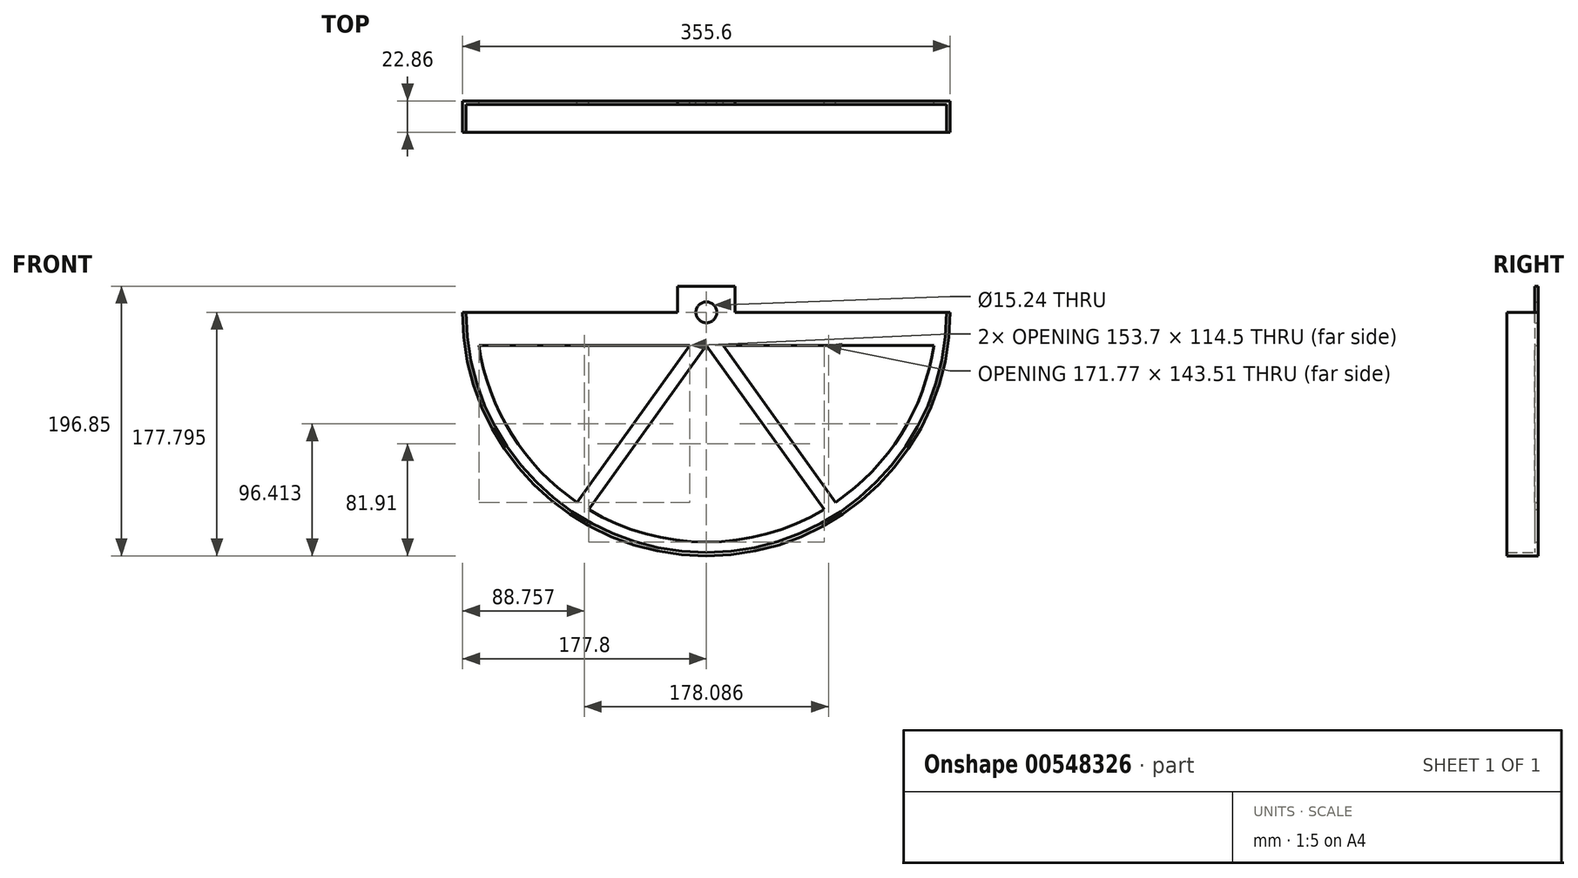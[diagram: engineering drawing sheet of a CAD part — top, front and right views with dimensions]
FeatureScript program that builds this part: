
annotation { "Feature Type Name" : "Feature", "Feature Type Description" : "" }
export const myFeature = defineFeature(function(context is Context, id is Id, definition is map)
    precondition{}
    {
        {
            var Q0;
            Q0=qCreatedBy(makeId("Front.planeOp"),FACE);
            var sketch = newSketch(context, id + "F0", { "sketchPlane" : qUnion([Q0])});
            skArc(sketch, "E0", {"start": v(-177.8, 177.3) * mm, "mid": v(0, -0.5) * mm, "end": v(177.8, 177.3) * mm});
            skLineSegment(sketch, "E1", {"start": v(0, 177.3) * mm, "end": v(177.8, 177.3) * mm});
            skLineSegment(sketch, "E2", {"start": v(0, 177.3) * mm, "end": v(-177.8, 177.3) * mm});
            skLineSegment(sketch, "E3.MirrorCS", {"start": v(-142.3, 159.18) * mm, "end": v(-142.3, 161.09) * mm});
            skLineSegment(sketch, "E4.MirrorCS", {"start": v(-166, 159.36) * mm, "end": v(-166.07, 161.26) * mm});
            skArc(sketch, "E5.MirrorCS", {"start": v(-169.1, 155.45) * mm, "mid": v(-160.47, 148.66) * mm, "end": v(-157.47, 159.21) * mm});
            skLineSegment(sketch, "E6.MirrorCS", {"start": v(-170.16, 157.27) * mm, "end": v(-168.5, 159.37) * mm});
            skLineSegment(sketch, "E7.MirrorCS", {"start": v(-174.1, 159.4) * mm, "end": v(-168.5, 159.37) * mm});
            skLineSegment(sketch, "E8.MirrorCS", {"start": v(-155.76, 159.25) * mm, "end": v(-142.3, 159.18) * mm});
            skLineSegment(sketch, "E9.MirrorCS", {"start": v(-142.3, 161.09) * mm, "end": v(-157.54, 161.16) * mm});
            skArc(sketch, "E10.MirrorCS", {"start": v(-170.16, 157.27) * mm, "mid": v(-161.42, 147.02) * mm, "end": v(-155.76, 159.25) * mm});
            skLineSegment(sketch, "E11.MirrorCS", {"start": v(-166.07, 161.26) * mm, "end": v(-174.53, 161.3) * mm});
            skLineSegment(sketch, "E12.MirrorCS", {"start": v(-166, 159.36) * mm, "end": v(-169.1, 155.45) * mm});
            skLineSegment(sketch, "E13", {"start": v(-174.1, 159.4) * mm, "end": v(-168.5, 129.1) * mm});
            skLineSegment(sketch, "E14", {"start": v(-162.95, 128.2) * mm, "end": v(-156.6, 98.59) * mm});
            skLineSegment(sketch, "E15.MirrorCS", {"start": v(-130.5, 132.86) * mm, "end": v(-130.84, 134.73) * mm});
            skLineSegment(sketch, "E16.MirrorCS", {"start": v(-154.75, 129.7) * mm, "end": v(-155.1, 131.58) * mm});
            skArc(sketch, "E17.MirrorCS", {"start": v(-157.1, 125.2) * mm, "mid": v(-148.27, 119.02) * mm, "end": v(-145.36, 129.4) * mm});
            skLineSegment(sketch, "E18.MirrorCS", {"start": v(-157.54, 129.03) * mm, "end": v(-157.45, 129.2) * mm});
            skLineSegment(sketch, "E19.MirrorCS", {"start": v(-162.95, 128.2) * mm, "end": v(-157.45, 129.2) * mm});
            skLineSegment(sketch, "E20.MirrorCS", {"start": v(-144.3, 130.3) * mm, "end": v(-130.5, 132.86) * mm});
            skLineSegment(sketch, "E21.MirrorCS", {"start": v(-130.84, 134.73) * mm, "end": v(-145.83, 131.96) * mm});
            skArc(sketch, "E22.MirrorCS", {"start": v(-157.54, 129.03) * mm, "mid": v(-149.72, 117.28) * mm, "end": v(-144.3, 130.3) * mm});
            skLineSegment(sketch, "E23.MirrorCS", {"start": v(-145.83, 131.96) * mm, "end": v(-145.36, 129.4) * mm});
            skLineSegment(sketch, "E24.MirrorCS", {"start": v(-155.1, 131.58) * mm, "end": v(-168.5, 129.1) * mm});
            skLineSegment(sketch, "E25.MirrorCS", {"start": v(-154.75, 129.7) * mm, "end": v(-157.1, 125.2) * mm});
            skLineSegment(sketch, "E26.MirrorCS", {"start": v(-119.21, 109.69) * mm, "end": v(-119.9, 111.46) * mm});
            skLineSegment(sketch, "E27.MirrorCS", {"start": v(-142.33, 102.07) * mm, "end": v(-143.02, 103.85) * mm});
            skArc(sketch, "E28.MirrorCS", {"start": v(-143.8, 97.2) * mm, "mid": v(-133.82, 93.07) * mm, "end": v(-133.3, 103.86) * mm});
            skLineSegment(sketch, "E29.MirrorCS", {"start": v(-145.22, 100.13) * mm, "end": v(-144.94, 101.06) * mm});
            skLineSegment(sketch, "E30.MirrorCS", {"start": v(-150.15, 99.04) * mm, "end": v(-144.94, 101.06) * mm});
            skLineSegment(sketch, "E31.MirrorCS", {"start": v(-132.1, 104.69) * mm, "end": v(-119.21, 109.69) * mm});
            skLineSegment(sketch, "E32.MirrorCS", {"start": v(-119.9, 111.46) * mm, "end": v(-134.1, 105.95) * mm});
            skArc(sketch, "E33.MirrorCS", {"start": v(-145.22, 100.13) * mm, "mid": v(-134.73, 91.1) * mm, "end": v(-132.1, 104.69) * mm});
            skLineSegment(sketch, "E34.MirrorCS", {"start": v(-134.1, 105.95) * mm, "end": v(-133.3, 103.86) * mm});
            skLineSegment(sketch, "E35.MirrorCS", {"start": v(-143.02, 103.85) * mm, "end": v(-156.6, 98.59) * mm});
            skLineSegment(sketch, "E36.MirrorCS", {"start": v(-142.33, 102.07) * mm, "end": v(-143.8, 97.2) * mm});
            skLineSegment(sketch, "E37", {"start": v(-174.53, 177.3) * mm, "end": v(-174.53, 161.3) * mm});
            skLineSegment(sketch, "E38", {"start": v(-150.15, 99.04) * mm, "end": v(-139.2, 70.82) * mm});
            skLineSegment(sketch, "E39", {"start": v(-174.53, 161.3) * mm, "end": v(0, 177.3) * mm, "construction": true});
            skLineSegment(sketch, "E40", {"start": v(-168.5, 129.1) * mm, "end": v(0, 177.3) * mm, "construction": true});
            skLineSegment(sketch, "E41", {"start": v(-156.6, 98.59) * mm, "end": v(0, 177.3) * mm, "construction": true});
            skLineSegment(sketch, "E42", {"start": v(-139.2, 70.82) * mm, "end": v(0, 177.3) * mm, "construction": true});
            skLineSegment(sketch, "E43", {"start": v(-174.1, 159.4) * mm, "end": v(-174.45, 161.3) * mm, "construction": true});
            skLineSegment(sketch, "E44", {"start": v(-162.95, 128.2) * mm, "end": v(-163.35, 130.05) * mm, "construction": true});
            skLineSegment(sketch, "E45", {"start": v(-150.15, 99.04) * mm, "end": v(-150.84, 100.82) * mm, "construction": true});
            skLineSegment(sketch, "E46", {"start": v(0, 177.3) * mm, "end": v(-116.96, 46.77) * mm, "construction": true});
            skLineSegment(sketch, "E47", {"start": v(-132.44, 72.79) * mm, "end": v(-116.96, 46.77) * mm});
            skLineSegment(sketch, "E48.MirrorCS", {"start": v(-88.28, 67.45) * mm, "end": v(-89.57, 68.85) * mm});
            skLineSegment(sketch, "E49.MirrorCS", {"start": v(-107.92, 52.51) * mm, "end": v(-109.2, 53.91) * mm});
            skArc(sketch, "E50.MirrorCS", {"start": v(-107.5, 47.45) * mm, "mid": v(-97.11, 46.67) * mm, "end": v(-98.9, 56.94) * mm});
            skLineSegment(sketch, "E51.MirrorCS", {"start": v(-109.3, 47.8) * mm, "end": v(-109.55, 51) * mm});
            skLineSegment(sketch, "E52.MirrorCS", {"start": v(-113.66, 47.22) * mm, "end": v(-109.55, 51) * mm});
            skLineSegment(sketch, "E53.MirrorCS", {"start": v(-98.31, 58.2) * mm, "end": v(-88.28, 67.45) * mm});
            skLineSegment(sketch, "E54.MirrorCS", {"start": v(-89.57, 68.85) * mm, "end": v(-100.78, 58.52) * mm});
            skLineSegment(sketch, "E55.MirrorCS", {"start": v(-109.2, 53.91) * mm, "end": v(-116.96, 46.77) * mm});
            skLineSegment(sketch, "E56.MirrorCS", {"start": v(-107.92, 52.51) * mm, "end": v(-107.5, 47.45) * mm});
            skLineSegment(sketch, "E57", {"start": v(-109.55, 51) * mm, "end": v(-98.31, 58.2) * mm, "construction": true});
            skLineSegment(sketch, "E58", {"start": v(-113.66, 47.22) * mm, "end": v(-90.63, 27.29) * mm});
            skLineSegment(sketch, "E59", {"start": v(-90.63, 27.29) * mm, "end": v(0, 177.3) * mm, "construction": true});
            skLineSegment(sketch, "E60.MirrorCS", {"start": v(-67.5, 53.57) * mm, "end": v(-69.03, 54.7) * mm});
            skLineSegment(sketch, "E61.MirrorCS", {"start": v(-82.81, 34.6) * mm, "end": v(-84.34, 35.75) * mm});
            skArc(sketch, "E62.MirrorCS", {"start": v(-81.47, 29.71) * mm, "mid": v(-70.86, 31.55) * mm, "end": v(-76.08, 40.96) * mm});
            skLineSegment(sketch, "E63.MirrorCS", {"start": v(-87.47, 28.34) * mm, "end": v(-84.14, 32.82) * mm});
            skLineSegment(sketch, "E64.MirrorCS", {"start": v(-75.85, 42.34) * mm, "end": v(-67.5, 53.57) * mm});
            skLineSegment(sketch, "E65.MirrorCS", {"start": v(-69.03, 54.7) * mm, "end": v(-78.12, 42.48) * mm});
            skArc(sketch, "E66.MirrorCS", {"start": v(-83.27, 29.68) * mm, "mid": v(-69.91, 30.35) * mm, "end": v(-75.85, 42.34) * mm});
            skLineSegment(sketch, "E67.MirrorCS", {"start": v(-78.12, 42.48) * mm, "end": v(-76.08, 40.96) * mm});
            skLineSegment(sketch, "E68.MirrorCS", {"start": v(-84.34, 35.75) * mm, "end": v(-90.63, 27.29) * mm});
            skLineSegment(sketch, "E69.MirrorCS", {"start": v(-82.81, 34.6) * mm, "end": v(-81.47, 29.71) * mm});
            skArc(sketch, "E70.trimOffspring", {"start": v(-109.3, 47.8) * mm, "mid": v(-96.5, 45.3) * mm, "end": v(-98.31, 58.2) * mm});
            skLineSegment(sketch, "E71", {"start": v(-82.81, 34.6) * mm, "end": v(-76.08, 40.96) * mm, "construction": true});
            skLineSegment(sketch, "E72", {"start": v(-84.14, 32.82) * mm, "end": v(-83.27, 29.68) * mm});
            skLineSegment(sketch, "E73.MirrorCS", {"start": v(-41.93, 43.33) * mm, "end": v(-43.64, 44.16) * mm});
            skLineSegment(sketch, "E74.MirrorCS", {"start": v(-54.81, 21.7) * mm, "end": v(-56.52, 22.52) * mm});
            skArc(sketch, "E75.MirrorCS", {"start": v(-52.58, 17.13) * mm, "mid": v(-43.55, 21.13) * mm, "end": v(-48.59, 29.62) * mm});
            skLineSegment(sketch, "E76.MirrorCS", {"start": v(-54.18, 16.42) * mm, "end": v(-55.78, 19.7) * mm});
            skLineSegment(sketch, "E77.MirrorCS", {"start": v(-58.23, 14.66) * mm, "end": v(-55.78, 19.7) * mm});
            skLineSegment(sketch, "E78.MirrorCS", {"start": v(-47.96, 30.92) * mm, "end": v(-41.93, 43.33) * mm});
            skLineSegment(sketch, "E79.MirrorCS", {"start": v(-43.64, 44.16) * mm, "end": v(-50.3, 30.46) * mm});
            skArc(sketch, "E80.MirrorCS", {"start": v(-54.18, 16.42) * mm, "mid": v(-42.49, 19.98) * mm, "end": v(-47.96, 30.92) * mm});
            skLineSegment(sketch, "E81.MirrorCS", {"start": v(-50.3, 30.46) * mm, "end": v(-48.59, 29.62) * mm});
            skLineSegment(sketch, "E82.MirrorCS", {"start": v(-56.52, 22.52) * mm, "end": v(-61.13, 13.04) * mm});
            skLineSegment(sketch, "E83.MirrorCS", {"start": v(-54.81, 21.7) * mm, "end": v(-52.58, 17.13) * mm});
            skLineSegment(sketch, "E84", {"start": v(0, 177.3) * mm, "end": v(-29.92, 2.03) * mm, "construction": true});
            skLineSegment(sketch, "E85", {"start": v(-58.23, 14.66) * mm, "end": v(-29.5, 4.54) * mm});
            skLineSegment(sketch, "E86", {"start": v(-55.78, 19.7) * mm, "end": v(-48.59, 29.62) * mm, "construction": true});
            skLineSegment(sketch, "E87", {"start": v(0, 177.3) * mm, "end": v(3.21, -0.48) * mm, "construction": true});
            skLineSegment(sketch, "E88", {"start": v(0, 177.3) * mm, "end": v(36.24, 3.23) * mm, "construction": true});
            skLineSegment(sketch, "E89", {"start": v(0, 177.3) * mm, "end": v(68, 13.01) * mm, "construction": true});
            skLineSegment(sketch, "E90", {"start": v(0, 177.3) * mm, "end": v(97.38, 28.54) * mm, "construction": true});
            skLineSegment(sketch, "E91", {"start": v(0, 177.3) * mm, "end": v(123.37, 49.26) * mm, "construction": true});
            skLineSegment(sketch, "E92", {"start": v(0, 177.3) * mm, "end": v(145.04, 74.45) * mm, "construction": true});
            skLineSegment(sketch, "E93.MirrorCS", {"start": v(-16.96, 36.4) * mm, "end": v(-18.8, 36.9) * mm});
            skLineSegment(sketch, "E94.MirrorCS", {"start": v(-24.9, 14.2) * mm, "end": v(-26.74, 14.7) * mm});
            skArc(sketch, "E95.MirrorCS", {"start": v(-21.85, 10.14) * mm, "mid": v(-11.66, 15.16) * mm, "end": v(-20.95, 21.7) * mm});
            skLineSegment(sketch, "E96.MirrorCS", {"start": v(-24.1, 10.23) * mm, "end": v(-25.48, 12.06) * mm});
            skLineSegment(sketch, "E97.MirrorCS", {"start": v(-26.94, 6.67) * mm, "end": v(-25.48, 12.06) * mm});
            skLineSegment(sketch, "E98.MirrorCS", {"start": v(-20.5, 23.35) * mm, "end": v(-16.96, 36.4) * mm});
            skLineSegment(sketch, "E99.MirrorCS", {"start": v(-18.8, 36.9) * mm, "end": v(-22.79, 22.2) * mm});
            skArc(sketch, "E100.MirrorCS", {"start": v(-24.1, 10.23) * mm, "mid": v(-10.53, 13.55) * mm, "end": v(-20.5, 23.35) * mm});
            skLineSegment(sketch, "E101.MirrorCS", {"start": v(-22.79, 22.2) * mm, "end": v(-20.95, 21.7) * mm});
            skLineSegment(sketch, "E102.MirrorCS", {"start": v(-26.74, 14.7) * mm, "end": v(-29.5, 4.54) * mm});
            skLineSegment(sketch, "E103.MirrorCS", {"start": v(-24.9, 14.2) * mm, "end": v(-21.85, 10.14) * mm});
            skLineSegment(sketch, "E104", {"start": v(-26.94, 6.67) * mm, "end": v(3.17, 2.06) * mm});
            skLineSegment(sketch, "E105", {"start": v(-25.48, 12.06) * mm, "end": v(-20.95, 21.7) * mm, "construction": true});
            skLineSegment(sketch, "E106", {"start": v(0, 177.3) * mm, "end": v(-61.13, 13.04) * mm, "construction": true});
            skLineSegment(sketch, "E107.MirrorCS", {"start": v(9.56, 35.7) * mm, "end": v(7.66, 35.86) * mm});
            skLineSegment(sketch, "E108.MirrorCS", {"start": v(5.89, 12.42) * mm, "end": v(3.99, 12.57) * mm});
            skArc(sketch, "E109.MirrorCS", {"start": v(9.64, 9) * mm, "mid": v(18.72, 15.82) * mm, "end": v(8.37, 20.51) * mm});
            skLineSegment(sketch, "E110.MirrorCS", {"start": v(7.4, 8.66) * mm, "end": v(5.71, 10.2) * mm});
            skLineSegment(sketch, "E111.MirrorCS", {"start": v(5.28, 4.64) * mm, "end": v(5.71, 10.2) * mm});
            skLineSegment(sketch, "E112.MirrorCS", {"start": v(8.5, 22.22) * mm, "end": v(9.56, 35.7) * mm});
            skLineSegment(sketch, "E113.MirrorCS", {"start": v(7.66, 35.86) * mm, "end": v(6.47, 20.66) * mm});
            skArc(sketch, "E114.MirrorCS", {"start": v(7.4, 8.66) * mm, "mid": v(20.13, 14.45) * mm, "end": v(8.5, 22.22) * mm});
            skLineSegment(sketch, "E115.MirrorCS", {"start": v(6.47, 20.66) * mm, "end": v(8.37, 20.51) * mm});
            skLineSegment(sketch, "E116.MirrorCS", {"start": v(3.99, 12.57) * mm, "end": v(3.17, 2.06) * mm});
            skLineSegment(sketch, "E117.MirrorCS", {"start": v(5.89, 12.42) * mm, "end": v(9.64, 9) * mm});
            skLineSegment(sketch, "E118", {"start": v(5.71, 10.2) * mm, "end": v(8.37, 20.51) * mm, "construction": true});
            skLineSegment(sketch, "E119", {"start": v(5.28, 4.64) * mm, "end": v(35.72, 5.71) * mm});
            skLineSegment(sketch, "E120.MirrorCS", {"start": v(35.74, 39.96) * mm, "end": v(33.85, 39.75) * mm});
            skLineSegment(sketch, "E121.MirrorCS", {"start": v(36.47, 16.4) * mm, "end": v(34.57, 16.2) * mm});
            skArc(sketch, "E122.MirrorCS", {"start": v(40.79, 13.73) * mm, "mid": v(48.44, 22.12) * mm, "end": v(37.4, 24.81) * mm});
            skLineSegment(sketch, "E123.MirrorCS", {"start": v(38.66, 12.99) * mm, "end": v(36.7, 14.19) * mm});
            skLineSegment(sketch, "E124.MirrorCS", {"start": v(37.32, 8.63) * mm, "end": v(36.7, 14.19) * mm});
            skLineSegment(sketch, "E125.MirrorCS", {"start": v(37.22, 26.51) * mm, "end": v(35.74, 39.96) * mm});
            skLineSegment(sketch, "E126.MirrorCS", {"start": v(33.85, 39.75) * mm, "end": v(35.5, 24.6) * mm});
            skArc(sketch, "E127.MirrorCS", {"start": v(38.66, 12.99) * mm, "mid": v(50.08, 21.04) * mm, "end": v(37.22, 26.51) * mm});
            skLineSegment(sketch, "E128.MirrorCS", {"start": v(35.5, 24.6) * mm, "end": v(37.4, 24.81) * mm});
            skLineSegment(sketch, "E129.MirrorCS", {"start": v(34.57, 16.2) * mm, "end": v(35.72, 5.71) * mm});
            skLineSegment(sketch, "E130.MirrorCS", {"start": v(36.47, 16.4) * mm, "end": v(40.79, 13.73) * mm});
            skLineSegment(sketch, "E131", {"start": v(36.7, 14.19) * mm, "end": v(37.4, 24.81) * mm, "construction": true});
            skLineSegment(sketch, "E132", {"start": v(37.32, 8.63) * mm, "end": v(67.03, 15.36) * mm});
            skLineSegment(sketch, "E133.MirrorCS", {"start": v(60.67, 49.01) * mm, "end": v(58.85, 48.45) * mm});
            skLineSegment(sketch, "E134.MirrorCS", {"start": v(65.77, 26) * mm, "end": v(63.95, 25.44) * mm});
            skArc(sketch, "E135.MirrorCS", {"start": v(70.51, 24.18) * mm, "mid": v(76.47, 33.85) * mm, "end": v(65.13, 34.44) * mm});
            skLineSegment(sketch, "E136.MirrorCS", {"start": v(68.56, 23.05) * mm, "end": v(66.42, 23.87) * mm});
            skLineSegment(sketch, "E137.MirrorCS", {"start": v(68.05, 18.53) * mm, "end": v(66.42, 23.87) * mm});
            skLineSegment(sketch, "E138.MirrorCS", {"start": v(64.63, 36.07) * mm, "end": v(60.67, 49.01) * mm});
            skLineSegment(sketch, "E139.MirrorCS", {"start": v(58.85, 48.45) * mm, "end": v(63.3, 33.88) * mm});
            skArc(sketch, "E140.MirrorCS", {"start": v(68.56, 23.05) * mm, "mid": v(78.29, 33.1) * mm, "end": v(64.63, 36.07) * mm});
            skLineSegment(sketch, "E141.MirrorCS", {"start": v(63.3, 33.88) * mm, "end": v(65.13, 34.44) * mm});
            skLineSegment(sketch, "E142.MirrorCS", {"start": v(63.95, 25.44) * mm, "end": v(67.03, 15.36) * mm});
            skLineSegment(sketch, "E143.MirrorCS", {"start": v(65.77, 26) * mm, "end": v(70.51, 24.18) * mm});
            skLineSegment(sketch, "E144", {"start": v(66.42, 23.87) * mm, "end": v(65.13, 34.44) * mm, "construction": true});
            skLineSegment(sketch, "E145", {"start": v(68.05, 18.53) * mm, "end": v(96, 30.66) * mm});
            skLineSegment(sketch, "E146.MirrorCS", {"start": v(83.49, 62.54) * mm, "end": v(81.8, 61.66) * mm});
            skLineSegment(sketch, "E147.MirrorCS", {"start": v(92.78, 40.88) * mm, "end": v(91.1, 40) * mm});
            skArc(sketch, "E148.MirrorCS", {"start": v(97.78, 39.97) * mm, "mid": v(101.83, 50.59) * mm, "end": v(90.57, 49.05) * mm});
            skLineSegment(sketch, "E149.MirrorCS", {"start": v(96.06, 38.5) * mm, "end": v(93.81, 38.91) * mm});
            skLineSegment(sketch, "E150.MirrorCS", {"start": v(96.41, 33.96) * mm, "end": v(93.81, 38.91) * mm});
            skLineSegment(sketch, "E151.MirrorCS", {"start": v(89.78, 50.57) * mm, "end": v(83.49, 62.54) * mm});
            skLineSegment(sketch, "E152.MirrorCS", {"start": v(81.8, 61.66) * mm, "end": v(88.89, 48.17) * mm});
            skArc(sketch, "E153.MirrorCS", {"start": v(96.06, 38.5) * mm, "mid": v(103.75, 50.18) * mm, "end": v(89.78, 50.57) * mm});
            skLineSegment(sketch, "E154.MirrorCS", {"start": v(88.89, 48.17) * mm, "end": v(90.57, 49.05) * mm});
            skLineSegment(sketch, "E155.MirrorCS", {"start": v(91.1, 40) * mm, "end": v(96, 30.66) * mm});
            skLineSegment(sketch, "E156.MirrorCS", {"start": v(92.78, 40.88) * mm, "end": v(97.78, 39.97) * mm});
            skLineSegment(sketch, "E157", {"start": v(93.81, 38.91) * mm, "end": v(90.57, 49.05) * mm, "construction": true});
            skLineSegment(sketch, "E158", {"start": v(96.41, 33.96) * mm, "end": v(121.6, 51.09) * mm});
            skLineSegment(sketch, "E159.MirrorCS", {"start": v(103.38, 80.08) * mm, "end": v(101.9, 78.9) * mm});
            skLineSegment(sketch, "E160.MirrorCS", {"start": v(116.54, 60.53) * mm, "end": v(115.05, 59.34) * mm});
            skArc(sketch, "E161.MirrorCS", {"start": v(121.62, 60.57) * mm, "mid": v(123.63, 71.75) * mm, "end": v(112.86, 68.15) * mm});
            skLineSegment(sketch, "E162.MirrorCS", {"start": v(120.21, 58.8) * mm, "end": v(117.93, 58.79) * mm});
            skLineSegment(sketch, "E163.MirrorCS", {"start": v(121.4, 54.4) * mm, "end": v(117.93, 58.79) * mm});
            skLineSegment(sketch, "E164.MirrorCS", {"start": v(111.8, 69.49) * mm, "end": v(103.38, 80.08) * mm});
            skLineSegment(sketch, "E165.MirrorCS", {"start": v(101.9, 78.9) * mm, "end": v(111.37, 66.96) * mm});
            skArc(sketch, "E166.MirrorCS", {"start": v(120.21, 58.8) * mm, "mid": v(125.6, 71.7) * mm, "end": v(111.8, 69.49) * mm});
            skLineSegment(sketch, "E167.MirrorCS", {"start": v(111.37, 66.96) * mm, "end": v(112.86, 68.15) * mm});
            skLineSegment(sketch, "E168.MirrorCS", {"start": v(115.05, 59.34) * mm, "end": v(121.6, 51.09) * mm});
            skLineSegment(sketch, "E169.MirrorCS", {"start": v(116.54, 60.53) * mm, "end": v(121.62, 60.57) * mm});
            skLineSegment(sketch, "E170", {"start": v(117.93, 58.79) * mm, "end": v(112.86, 68.15) * mm, "construction": true});
            skLineSegment(sketch, "E171", {"start": v(121.4, 54.4) * mm, "end": v(142.97, 75.92) * mm});
            skLineSegment(sketch, "E172", {"start": v(142.97, 75.92) * mm, "end": v(96.82, 115.8) * mm});
            skLineSegment(sketch, "E173.MirrorCS", {"start": v(119.67, 101.02) * mm, "end": v(118.42, 99.58) * mm});
            skLineSegment(sketch, "E174.MirrorCS", {"start": v(136.24, 84.26) * mm, "end": v(135, 82.82) * mm});
            skArc(sketch, "E175.MirrorCS", {"start": v(141.22, 85.24) * mm, "mid": v(141.11, 96.6) * mm, "end": v(131.2, 91.06) * mm});
            skLineSegment(sketch, "E176.MirrorCS", {"start": v(140.17, 83.25) * mm, "end": v(137.92, 82.8) * mm});
            skLineSegment(sketch, "E177.MirrorCS", {"start": v(142.15, 79.15) * mm, "end": v(137.92, 82.8) * mm});
            skLineSegment(sketch, "E178.MirrorCS", {"start": v(129.9, 92.17) * mm, "end": v(119.67, 101.02) * mm});
            skLineSegment(sketch, "E179.MirrorCS", {"start": v(118.42, 99.58) * mm, "end": v(129.95, 89.61) * mm});
            skArc(sketch, "E180.MirrorCS", {"start": v(140.17, 83.25) * mm, "mid": v(143.05, 96.92) * mm, "end": v(129.9, 92.17) * mm});
            skLineSegment(sketch, "E181.MirrorCS", {"start": v(129.95, 89.61) * mm, "end": v(131.2, 91.06) * mm});
            skLineSegment(sketch, "E182.MirrorCS", {"start": v(135, 82.82) * mm, "end": v(142.97, 75.92) * mm});
            skLineSegment(sketch, "E183.MirrorCS", {"start": v(136.24, 84.26) * mm, "end": v(141.22, 85.24) * mm});
            skLineSegment(sketch, "E184", {"start": v(137.92, 82.8) * mm, "end": v(131.2, 91.06) * mm, "construction": true});
            skLineSegment(sketch, "E185", {"start": v(0, 177.3) * mm, "end": v(161.64, 103.24) * mm, "construction": true});
            skLineSegment(sketch, "E186", {"start": v(0, 177.3) * mm, "end": v(172.6, 134.62) * mm, "construction": true});
            skLineSegment(sketch, "E187", {"start": v(142.15, 79.15) * mm, "end": v(159.33, 104.3) * mm});
            skLineSegment(sketch, "E188.MirrorCS", {"start": v(127.38, 127.17) * mm, "end": v(126.42, 125.52) * mm});
            skLineSegment(sketch, "E189.MirrorCS", {"start": v(151.17, 111.23) * mm, "end": v(150.22, 109.59) * mm});
            skArc(sketch, "E190.MirrorCS", {"start": v(155.89, 113.13) * mm, "mid": v(153.67, 124.27) * mm, "end": v(144.96, 116.98) * mm});
            skLineSegment(sketch, "E191.MirrorCS", {"start": v(155.22, 110.97) * mm, "end": v(153.1, 110.12) * mm});
            skLineSegment(sketch, "E192.MirrorCS", {"start": v(157.93, 107.32) * mm, "end": v(153.1, 110.12) * mm});
            skLineSegment(sketch, "E193.MirrorCS", {"start": v(143.47, 117.84) * mm, "end": v(127.38, 127.17) * mm});
            skLineSegment(sketch, "E194.MirrorCS", {"start": v(126.42, 125.52) * mm, "end": v(144, 115.33) * mm});
            skArc(sketch, "E195.MirrorCS", {"start": v(155.22, 110.97) * mm, "mid": v(155.51, 124.95) * mm, "end": v(143.47, 117.84) * mm});
            skLineSegment(sketch, "E196.MirrorCS", {"start": v(144, 115.33) * mm, "end": v(144.96, 116.98) * mm});
            skLineSegment(sketch, "E197.MirrorCS", {"start": v(150.22, 109.59) * mm, "end": v(159.33, 104.3) * mm});
            skLineSegment(sketch, "E198.MirrorCS", {"start": v(151.17, 111.23) * mm, "end": v(155.89, 113.13) * mm});
            skLineSegment(sketch, "E199", {"start": v(153.1, 110.12) * mm, "end": v(144.96, 116.98) * mm, "construction": true});
            skLineSegment(sketch, "E200", {"start": v(157.93, 107.32) * mm, "end": v(170.14, 135.22) * mm});
            skLineSegment(sketch, "E201.MirrorCS", {"start": v(139.27, 150.07) * mm, "end": v(138.64, 148.27) * mm});
            skLineSegment(sketch, "E202.MirrorCS", {"start": v(160.82, 140.52) * mm, "end": v(160.2, 138.72) * mm});
            skArc(sketch, "E203.MirrorCS", {"start": v(165.1, 143.26) * mm, "mid": v(160.85, 153.8) * mm, "end": v(153.65, 145) * mm});
            skLineSegment(sketch, "E204.MirrorCS", {"start": v(164.85, 141.02) * mm, "end": v(162.92, 139.78) * mm});
            skLineSegment(sketch, "E205.MirrorCS", {"start": v(168.2, 137.93) * mm, "end": v(162.92, 139.78) * mm});
            skLineSegment(sketch, "E206.MirrorCS", {"start": v(152.03, 145.57) * mm, "end": v(139.27, 150.07) * mm});
            skLineSegment(sketch, "E207.MirrorCS", {"start": v(138.64, 148.27) * mm, "end": v(153.02, 143.2) * mm});
            skArc(sketch, "E208.MirrorCS", {"start": v(164.85, 141.02) * mm, "mid": v(162.54, 154.8) * mm, "end": v(152.03, 145.57) * mm});
            skLineSegment(sketch, "E209.MirrorCS", {"start": v(153.02, 143.2) * mm, "end": v(153.65, 145) * mm});
            skLineSegment(sketch, "E210.MirrorCS", {"start": v(160.2, 138.72) * mm, "end": v(170.14, 135.22) * mm});
            skLineSegment(sketch, "E211.MirrorCS", {"start": v(160.82, 140.52) * mm, "end": v(165.1, 143.26) * mm});
            skLineSegment(sketch, "E212", {"start": v(162.92, 139.78) * mm, "end": v(153.65, 145) * mm, "construction": true});
            skLineSegment(sketch, "E213", {"start": v(0, 177.3) * mm, "end": v(177.53, 167.48) * mm, "construction": true});
            skLineSegment(sketch, "E214", {"start": v(168.2, 137.93) * mm, "end": v(175, 167.62) * mm});
            skLineSegment(sketch, "E215", {"start": v(175, 167.62) * mm, "end": v(175, 177.3) * mm});
            skLineSegment(sketch, "E216", {"start": v(-87.47, 28.34) * mm, "end": v(-61.13, 13.04) * mm});
            skLineSegment(sketch, "E217", {"start": v(-20.86, 177.3) * mm, "end": v(-20.86, 196.35) * mm});
            skCircle(sketch, "E218", {"center": v(0, 177.3) * mm, "radius": 7.62 * mm});
            skLineSegment(sketch, "E219.MirrorCS", {"start": v(-105.56, 87.5) * mm, "end": v(-106.56, 89.12) * mm});
            skLineSegment(sketch, "E220.MirrorCS", {"start": v(-125.85, 76.9) * mm, "end": v(-126.85, 78.51) * mm});
            skArc(sketch, "E221.MirrorCS", {"start": v(-126.39, 71.85) * mm, "mid": v(-115.2, 68.69) * mm, "end": v(-118.7, 79.77) * mm});
            skLineSegment(sketch, "E222.MirrorCS", {"start": v(-127.8, 74.76) * mm, "end": v(-127.7, 75.74) * mm});
            skLineSegment(sketch, "E223.MirrorCS", {"start": v(-132.44, 72.79) * mm, "end": v(-127.7, 75.74) * mm});
            skLineSegment(sketch, "E224.MirrorCS", {"start": v(-116.66, 80.58) * mm, "end": v(-105.56, 87.5) * mm});
            skLineSegment(sketch, "E225.MirrorCS", {"start": v(-106.56, 89.12) * mm, "end": v(-119.5, 81.06) * mm});
            skArc(sketch, "E226.MirrorCS", {"start": v(-127.8, 74.76) * mm, "mid": v(-116.24, 66.2) * mm, "end": v(-116.66, 80.58) * mm});
            skLineSegment(sketch, "E227.MirrorCS", {"start": v(-119.5, 81.06) * mm, "end": v(-118.7, 79.77) * mm});
            skLineSegment(sketch, "E228.MirrorCS", {"start": v(-126.85, 78.51) * mm, "end": v(-139.2, 70.82) * mm});
            skLineSegment(sketch, "E229.MirrorCS", {"start": v(-125.85, 76.9) * mm, "end": v(-126.39, 71.85) * mm});
            skLineSegment(sketch, "E230", {"start": v(-98.9, 56.94) * mm, "end": v(-100.78, 58.52) * mm});
            skLineSegment(sketch, "E231", {"start": v(-20.86, 196.35) * mm, "end": v(0, 196.35) * mm});
            skLineSegment(sketch, "E232.MirrorCS", {"start": v(20.86, 196.35) * mm, "end": v(0, 196.35) * mm});
            skLineSegment(sketch, "E233.MirrorCS", {"start": v(20.86, 177.3) * mm, "end": v(20.86, 196.35) * mm});
            skLineSegment(sketch, "E234", {"start": v(-157.47, 159.21) * mm, "end": v(-157.54, 161.16) * mm});
            skSolve(sketch);
        }
        {
            var Q0;
            Q0=qSketchRegion(id+"F0",true);
            extrude(context, id + "F1", {"entities" : qUnion([Q0]), "endBound" : BoundingType.SYMMETRIC, "depth" : 50.8 * mm, "offsetDistance" : 25.4 * mm});
        }
        {
            var Q0;
            Q0=makeQuery(id+"F1.opExtrude","SWEPT_FACE",FACE,{"disambiguationData":[OSD([sQuery(id+"F0.wireOp",EDGE,"E1"),sQuery(id+"F0.wireOp",EDGE,"E2")])]});
            var Q1;
            Q1=makeQuery(id+"F1.opExtrude","SWEPT_FACE",FACE,{"disambiguationData":[OSD([sQuery(id+"F0.wireOp",EDGE,"E217")])]});
            var Q2;
            Q2=makeQuery(id+"F1.opExtrude","SWEPT_FACE",FACE,{"disambiguationData":[OSD([sQuery(id+"F0.wireOp",EDGE,"IKzNIRuS-lt9D-PZX5-G1JW-kbrlMgvdaDML")])]});
            var Q3;
            Q3=makeQuery(id+"F1.opExtrude","SWEPT_FACE",FACE,{"disambiguationData":[OSD([sQuery(id+"F0.wireOp",EDGE,"ju7AKv3p-tV9e-Mq4A-qTnI-Takg7eoSyEy9")])]});
            shell(context, id + "F2", {"entities" : qUnion([Q0, Q1, Q2, Q3]), "thickness" : 2.54 * mm});
        }
        {
            var Q0;
            {var subQ0=sQuery(id+"F0.wireOp",EDGE,"8sBSUSAj-00hb-c3g1-GJDK-NZvKGYPpUrdB");Q0=makeQuery(id+"F0.imprint","IMPRINT",FACE,{"disambiguationData":[TD([[makeQuery(id+"F0.imprint","IMPRINT",EDGE,{"derivedFrom":subQ0}),-1.0]])]});}
            var Q1;
            Q1=makeQuery(id+"F0.imprint","IMPRINT",FACE,{"disambiguationData":[TD([[makeQuery(id+"F0.imprint","IMPRINT",EDGE,{"derivedFrom":sQuery(id+"F0.wireOp",EDGE,"E3.MirrorCS")}),1.0]])]});
            extrude(context, id + "F3", {"entities" : qUnion([Q0, Q1]), "operationType" : NewBodyOperationType.ADD, "endBound" : BoundingType.SYMMETRIC, "depth" : 5.08 * mm, "offsetDistance" : 25.4 * mm});
        }
        {
            var Q0;
            Q0=makeQuery(id+"F1.opExtrude","CAP_FACE",FACE,{"disambiguationData":[OSD([sQuery(id+"F0.wireOp",EDGE,"E0"),sQuery(id+"F0.wireOp",EDGE,"E1"),sQuery(id+"F0.wireOp",EDGE,"E2"),sQuery(id+"F0.wireOp",EDGE,"4NdIO9du-pqLB-0gZj-tUX9-g2KgcOWVYO3W")])],"isStart":false});
            var sketch = newSketch(context, id + "F4", { "sketchPlane" : qUnion([Q0])});
            skArc(sketch, "E235.0", {"start": v(-166.8, 160.57) * mm, "mid": v(-144.76, 92.76) * mm, "end": v(-96.53, 40.24) * mm});
            skLineSegment(sketch, "E236", {"start": v(0, 153.17) * mm, "end": v(-84.49, 32.5) * mm});
            skLineSegment(sketch, "E237", {"start": v(-12.28, 160.57) * mm, "end": v(-96.53, 40.24) * mm});
            skLineSegment(sketch, "E238", {"start": v(-12.28, 160.57) * mm, "end": v(-166.8, 160.57) * mm});
            skLineSegment(sketch, "E239.MirrorCS", {"start": v(12.2, 160.53) * mm, "end": v(166.8, 160.57) * mm});
            skLineSegment(sketch, "E240.MirrorCS", {"start": v(0, 153.17) * mm, "end": v(84.49, 32.5) * mm});
            skLineSegment(sketch, "E241.MirrorCS", {"start": v(12.2, 160.53) * mm, "end": v(96.53, 40.24) * mm});
            skArc(sketch, "E242.trimOffspring", {"start": v(-84.49, 32.5) * mm, "mid": v(0, 9.66) * mm, "end": v(84.49, 32.5) * mm});
            skArc(sketch, "E243.trimOffspring", {"start": v(96.53, 40.24) * mm, "mid": v(144.76, 92.76) * mm, "end": v(166.8, 160.57) * mm});
            skSolve(sketch);
        }
        {
            var Q0;
            Q0=qSketchRegion(id+"F4",true);
            extrude(context, id + "F5", {"entities" : qUnion([Q0]), "operationType" : NewBodyOperationType.REMOVE, "endBound" : BoundingType.UP_TO_NEXT, "oppositeDirection" : true, "depth" : 25.4 * mm, "offsetDistance" : 25.4 * mm});
        }
        {
            var Q0;
            Q0=makeQuery(id+"F1.opExtrude","CAP_FACE",FACE,{"disambiguationData":[OSD([sQuery(id+"F0.wireOp",EDGE,"E0"),sQuery(id+"F0.wireOp",EDGE,"E1"),sQuery(id+"F0.wireOp",EDGE,"E2"),sQuery(id+"F0.wireOp",EDGE,"E217"),sQuery(id+"F0.wireOp",EDGE,"E218"),sQuery(id+"F0.wireOp",EDGE,"E231"),sQuery(id+"F0.wireOp",EDGE,"E232.MirrorCS"),sQuery(id+"F0.wireOp",EDGE,"E233.MirrorCS")])],"isStart":true});
            var sketch = newSketch(context, id + "F6", { "sketchPlane" : qUnion([Q0])});
            skArc(sketch, "E244.0", {"start": v(165.9, 153.17) * mm, "mid": v(142.12, 88.38) * mm, "end": v(94.25, 38.66) * mm});
            skLineSegment(sketch, "E245", {"start": v(0, 153.17) * mm, "end": v(-85.88, 33.33) * mm});
            skLineSegment(sketch, "E246", {"start": v(-12.2, 153.17) * mm, "end": v(-94.25, 38.66) * mm});
            skLineSegment(sketch, "E247", {"start": v(-12.2, 153.17) * mm, "end": v(-165.9, 153.17) * mm});
            skLineSegment(sketch, "E248.MirrorCS", {"start": v(0, 153.17) * mm, "end": v(85.88, 33.33) * mm});
            skLineSegment(sketch, "E249.MirrorCS", {"start": v(12.2, 153.17) * mm, "end": v(94.25, 38.66) * mm});
            skLineSegment(sketch, "E250.MirrorCS", {"start": v(12.2, 153.17) * mm, "end": v(165.9, 153.17) * mm});
            skArc(sketch, "E251.trimOffspring", {"start": v(-94.25, 38.66) * mm, "mid": v(-142.12, 88.38) * mm, "end": v(-165.9, 153.17) * mm});
            skArc(sketch, "E252.trimOffspring", {"start": v(85.88, 33.33) * mm, "mid": v(0, 9.66) * mm, "end": v(-85.88, 33.33) * mm});
            skSolve(sketch);
        }
        {
            var Q0;
            Q0=qSketchRegion(id+"F6",true);
            extrude(context, id + "F7", {"entities" : qUnion([Q0]), "operationType" : NewBodyOperationType.REMOVE, "endBound" : BoundingType.UP_TO_NEXT, "oppositeDirection" : true, "depth" : 25.4 * mm, "offsetDistance" : 25.4 * mm});
        }
        {
            var Q0;
            Q0=makeQuery(id+"F1.opExtrude","SWEPT_FACE",FACE,{"disambiguationData":[OSD([sQuery(id+"F0.wireOp",EDGE,"E233.MirrorCS")])]});
            var sketch = newSketch(context, id + "F8", { "sketchPlane" : qUnion([Q0])});
            skLineSegment(sketch, "E253", {"start": v(-22.86, 177.3) * mm, "end": v(-22.86, 196.35) * mm});
            skLineSegment(sketch, "E254", {"start": v(-22.86, 196.35) * mm, "end": v(22.86, 196.35) * mm});
            skLineSegment(sketch, "E255", {"start": v(22.86, 196.35) * mm, "end": v(22.86, 177.3) * mm});
            skLineSegment(sketch, "E256", {"start": v(22.86, 177.3) * mm, "end": v(22.86, 161.97) * mm});
            skLineSegment(sketch, "E257", {"start": v(22.86, 161.97) * mm, "end": v(-22.86, 161.97) * mm});
            skLineSegment(sketch, "E258", {"start": v(-22.86, 161.97) * mm, "end": v(-22.86, 177.3) * mm});
            skSolve(sketch);
        }
        {
            var Q0;
            Q0=makeQuery(id+"F8.imprint","IMPRINT",FACE,{"disambiguationData":[TD([[makeQuery(id+"F8.imprint","IMPRINT",EDGE,{"derivedFrom":sQuery(id+"F8.wireOp",EDGE,"E256")}),-1.0]])]});
            var Q1;
            Q1=makeQuery(id+"F8.imprint","IMPRINT",FACE,{"disambiguationData":[TD([[makeQuery(id+"F8.imprint","IMPRINT",EDGE,{"derivedFrom":sQuery(id+"F8.wireOp",EDGE,"E253")}),-1.0]])]});
            extrude(context, id + "F9", {"entities" : qUnion([Q0, Q1]), "operationType" : NewBodyOperationType.REMOVE, "oppositeDirection" : true, "depth" : 52.07 * mm, "offsetDistance" : 25.4 * mm});
        }
        {
            var Q0;
            Q0=makeQuery(id+"F1.opExtrude","CAP_FACE",FACE,{"disambiguationData":[OSD([sQuery(id+"F0.wireOp",EDGE,"E0"),sQuery(id+"F0.wireOp",EDGE,"E1"),sQuery(id+"F0.wireOp",EDGE,"E2"),sQuery(id+"F0.wireOp",EDGE,"E217"),sQuery(id+"F0.wireOp",EDGE,"E218"),sQuery(id+"F0.wireOp",EDGE,"E231"),sQuery(id+"F0.wireOp",EDGE,"E232.MirrorCS"),sQuery(id+"F0.wireOp",EDGE,"E233.MirrorCS")])],"isStart":false});
            var sketch = newSketch(context, id + "F10", { "sketchPlane" : qUnion([Q0])});
            skLineSegment(sketch, "E259.bottom", {"start": v(-246.98, 230.1) * mm, "end": v(251.85, 230.1) * mm});
            skLineSegment(sketch, "E259.top", {"start": v(-246.98, -55.14) * mm, "end": v(251.85, -55.14) * mm});
            skLineSegment(sketch, "E259.left", {"start": v(-246.98, 230.1) * mm, "end": v(-246.98, -55.14) * mm});
            skLineSegment(sketch, "E259.right", {"start": v(251.85, 230.1) * mm, "end": v(251.85, -55.14) * mm});
            skSolve(sketch);
        }
        {
            var Q0;
            Q0=qSketchRegion(id+"F10",true);
            var Q1;
            {var subQ0=sQuery(id+"F0.wireOp",EDGE,"E223.MirrorCS");var subQ1=sQuery(id+"F0.wireOp",EDGE,"E222.MirrorCS");var subQ2=sQuery(id+"F0.wireOp",EDGE,"E220.MirrorCS");var subQ3=sQuery(id+"F0.wireOp",EDGE,"E55.MirrorCS");var subQ4=sQuery(id+"F0.wireOp",EDGE,"E219.MirrorCS");var subQ5=sQuery(id+"F0.wireOp",EDGE,"E221.MirrorCS");var subQ6=sQuery(id+"F0.wireOp",EDGE,"E229.MirrorCS");var subQ7=sQuery(id+"F0.wireOp",EDGE,"E228.MirrorCS");var subQ8=sQuery(id+"F0.wireOp",EDGE,"E227.MirrorCS");var subQ9=sQuery(id+"F0.wireOp",EDGE,"E226.MirrorCS");var subQ10=sQuery(id+"F0.wireOp",EDGE,"E225.MirrorCS");var subQ11=sQuery(id+"F0.wireOp",EDGE,"E224.MirrorCS");var subQ12=sQuery(id+"F0.wireOp",EDGE,"E47");var subQ13=sQuery(id+"F0.wireOp",EDGE,"E38");var subQ14=sQuery(id+"F0.wireOp",EDGE,"E0");var subQ15=makeQuery(id+"F3.opExtrude","CAP_FACE",FACE,{"disambiguationData":[OSD([subQ14,sQuery(id+"F0.wireOp",EDGE,"E1"),sQuery(id+"F0.wireOp",EDGE,"E2"),sQuery(id+"F0.wireOp",EDGE,"E3.MirrorCS"),sQuery(id+"F0.wireOp",EDGE,"E4.MirrorCS"),sQuery(id+"F0.wireOp",EDGE,"E5.MirrorCS"),sQuery(id+"F0.wireOp",EDGE,"E6.MirrorCS"),sQuery(id+"F0.wireOp",EDGE,"E7.MirrorCS"),sQuery(id+"F0.wireOp",EDGE,"E8.MirrorCS"),sQuery(id+"F0.wireOp",EDGE,"E9.MirrorCS"),sQuery(id+"F0.wireOp",EDGE,"E10.MirrorCS"),sQuery(id+"F0.wireOp",EDGE,"E11.MirrorCS"),sQuery(id+"F0.wireOp",EDGE,"E12.MirrorCS"),sQuery(id+"F0.wireOp",EDGE,"E13"),sQuery(id+"F0.wireOp",EDGE,"E14"),sQuery(id+"F0.wireOp",EDGE,"E15.MirrorCS"),sQuery(id+"F0.wireOp",EDGE,"E16.MirrorCS"),sQuery(id+"F0.wireOp",EDGE,"E17.MirrorCS"),sQuery(id+"F0.wireOp",EDGE,"E18.MirrorCS"),sQuery(id+"F0.wireOp",EDGE,"E19.MirrorCS"),sQuery(id+"F0.wireOp",EDGE,"E20.MirrorCS"),sQuery(id+"F0.wireOp",EDGE,"E21.MirrorCS"),sQuery(id+"F0.wireOp",EDGE,"E22.MirrorCS"),sQuery(id+"F0.wireOp",EDGE,"E23.MirrorCS"),sQuery(id+"F0.wireOp",EDGE,"E24.MirrorCS"),sQuery(id+"F0.wireOp",EDGE,"E25.MirrorCS"),sQuery(id+"F0.wireOp",EDGE,"E26.MirrorCS"),sQuery(id+"F0.wireOp",EDGE,"E27.MirrorCS"),sQuery(id+"F0.wireOp",EDGE,"E28.MirrorCS"),sQuery(id+"F0.wireOp",EDGE,"E29.MirrorCS"),sQuery(id+"F0.wireOp",EDGE,"E30.MirrorCS"),sQuery(id+"F0.wireOp",EDGE,"E31.MirrorCS"),sQuery(id+"F0.wireOp",EDGE,"E32.MirrorCS"),sQuery(id+"F0.wireOp",EDGE,"E33.MirrorCS"),sQuery(id+"F0.wireOp",EDGE,"E34.MirrorCS"),sQuery(id+"F0.wireOp",EDGE,"E35.MirrorCS"),sQuery(id+"F0.wireOp",EDGE,"E36.MirrorCS"),sQuery(id+"F0.wireOp",EDGE,"E37"),subQ13,subQ12,sQuery(id+"F0.wireOp",EDGE,"E48.MirrorCS"),sQuery(id+"F0.wireOp",EDGE,"E49.MirrorCS"),sQuery(id+"F0.wireOp",EDGE,"E50.MirrorCS"),sQuery(id+"F0.wireOp",EDGE,"E51.MirrorCS"),sQuery(id+"F0.wireOp",EDGE,"E52.MirrorCS"),sQuery(id+"F0.wireOp",EDGE,"E53.MirrorCS"),sQuery(id+"F0.wireOp",EDGE,"E54.MirrorCS"),subQ3,sQuery(id+"F0.wireOp",EDGE,"E56.MirrorCS"),sQuery(id+"F0.wireOp",EDGE,"E58"),sQuery(id+"F0.wireOp",EDGE,"E60.MirrorCS"),sQuery(id+"F0.wireOp",EDGE,"E61.MirrorCS"),sQuery(id+"F0.wireOp",EDGE,"E62.MirrorCS"),sQuery(id+"F0.wireOp",EDGE,"E63.MirrorCS"),sQuery(id+"F0.wireOp",EDGE,"E64.MirrorCS"),sQuery(id+"F0.wireOp",EDGE,"E65.MirrorCS"),sQuery(id+"F0.wireOp",EDGE,"E66.MirrorCS"),sQuery(id+"F0.wireOp",EDGE,"E67.MirrorCS"),sQuery(id+"F0.wireOp",EDGE,"E68.MirrorCS"),sQuery(id+"F0.wireOp",EDGE,"E69.MirrorCS"),sQuery(id+"F0.wireOp",EDGE,"E70.trimOffspring"),sQuery(id+"F0.wireOp",EDGE,"E72"),sQuery(id+"F0.wireOp",EDGE,"E73.MirrorCS"),sQuery(id+"F0.wireOp",EDGE,"E74.MirrorCS"),sQuery(id+"F0.wireOp",EDGE,"E75.MirrorCS"),sQuery(id+"F0.wireOp",EDGE,"E76.MirrorCS"),sQuery(id+"F0.wireOp",EDGE,"E77.MirrorCS"),sQuery(id+"F0.wireOp",EDGE,"E78.MirrorCS"),sQuery(id+"F0.wireOp",EDGE,"E79.MirrorCS"),sQuery(id+"F0.wireOp",EDGE,"E80.MirrorCS"),sQuery(id+"F0.wireOp",EDGE,"E81.MirrorCS"),sQuery(id+"F0.wireOp",EDGE,"E82.MirrorCS"),sQuery(id+"F0.wireOp",EDGE,"E83.MirrorCS"),sQuery(id+"F0.wireOp",EDGE,"E85"),sQuery(id+"F0.wireOp",EDGE,"E93.MirrorCS"),sQuery(id+"F0.wireOp",EDGE,"E94.MirrorCS"),sQuery(id+"F0.wireOp",EDGE,"E95.MirrorCS"),sQuery(id+"F0.wireOp",EDGE,"E96.MirrorCS"),sQuery(id+"F0.wireOp",EDGE,"E97.MirrorCS"),sQuery(id+"F0.wireOp",EDGE,"E98.MirrorCS"),sQuery(id+"F0.wireOp",EDGE,"E99.MirrorCS"),sQuery(id+"F0.wireOp",EDGE,"E100.MirrorCS"),sQuery(id+"F0.wireOp",EDGE,"E101.MirrorCS"),sQuery(id+"F0.wireOp",EDGE,"E102.MirrorCS"),sQuery(id+"F0.wireOp",EDGE,"E103.MirrorCS"),sQuery(id+"F0.wireOp",EDGE,"E104"),sQuery(id+"F0.wireOp",EDGE,"E107.MirrorCS"),sQuery(id+"F0.wireOp",EDGE,"E108.MirrorCS"),sQuery(id+"F0.wireOp",EDGE,"E109.MirrorCS"),sQuery(id+"F0.wireOp",EDGE,"E110.MirrorCS"),sQuery(id+"F0.wireOp",EDGE,"E111.MirrorCS"),sQuery(id+"F0.wireOp",EDGE,"E112.MirrorCS"),sQuery(id+"F0.wireOp",EDGE,"E113.MirrorCS"),sQuery(id+"F0.wireOp",EDGE,"E114.MirrorCS"),sQuery(id+"F0.wireOp",EDGE,"E115.MirrorCS"),sQuery(id+"F0.wireOp",EDGE,"E116.MirrorCS"),sQuery(id+"F0.wireOp",EDGE,"E117.MirrorCS"),sQuery(id+"F0.wireOp",EDGE,"E119"),sQuery(id+"F0.wireOp",EDGE,"E120.MirrorCS"),sQuery(id+"F0.wireOp",EDGE,"E121.MirrorCS"),sQuery(id+"F0.wireOp",EDGE,"E122.MirrorCS"),sQuery(id+"F0.wireOp",EDGE,"E123.MirrorCS"),sQuery(id+"F0.wireOp",EDGE,"E124.MirrorCS"),sQuery(id+"F0.wireOp",EDGE,"E125.MirrorCS"),sQuery(id+"F0.wireOp",EDGE,"E126.MirrorCS"),sQuery(id+"F0.wireOp",EDGE,"E127.MirrorCS"),sQuery(id+"F0.wireOp",EDGE,"E128.MirrorCS"),sQuery(id+"F0.wireOp",EDGE,"E129.MirrorCS"),sQuery(id+"F0.wireOp",EDGE,"E130.MirrorCS"),sQuery(id+"F0.wireOp",EDGE,"E132"),sQuery(id+"F0.wireOp",EDGE,"E133.MirrorCS"),sQuery(id+"F0.wireOp",EDGE,"E134.MirrorCS"),sQuery(id+"F0.wireOp",EDGE,"E135.MirrorCS"),sQuery(id+"F0.wireOp",EDGE,"E136.MirrorCS"),sQuery(id+"F0.wireOp",EDGE,"E137.MirrorCS"),sQuery(id+"F0.wireOp",EDGE,"E138.MirrorCS"),sQuery(id+"F0.wireOp",EDGE,"E139.MirrorCS"),sQuery(id+"F0.wireOp",EDGE,"E140.MirrorCS"),sQuery(id+"F0.wireOp",EDGE,"E141.MirrorCS"),sQuery(id+"F0.wireOp",EDGE,"E142.MirrorCS"),sQuery(id+"F0.wireOp",EDGE,"E143.MirrorCS"),sQuery(id+"F0.wireOp",EDGE,"E145"),sQuery(id+"F0.wireOp",EDGE,"E146.MirrorCS"),sQuery(id+"F0.wireOp",EDGE,"E147.MirrorCS"),sQuery(id+"F0.wireOp",EDGE,"E148.MirrorCS"),sQuery(id+"F0.wireOp",EDGE,"E149.MirrorCS"),sQuery(id+"F0.wireOp",EDGE,"E150.MirrorCS"),sQuery(id+"F0.wireOp",EDGE,"E151.MirrorCS"),sQuery(id+"F0.wireOp",EDGE,"E152.MirrorCS"),sQuery(id+"F0.wireOp",EDGE,"E153.MirrorCS"),sQuery(id+"F0.wireOp",EDGE,"E154.MirrorCS"),sQuery(id+"F0.wireOp",EDGE,"E155.MirrorCS"),sQuery(id+"F0.wireOp",EDGE,"E156.MirrorCS"),sQuery(id+"F0.wireOp",EDGE,"E158"),sQuery(id+"F0.wireOp",EDGE,"E159.MirrorCS"),sQuery(id+"F0.wireOp",EDGE,"E160.MirrorCS"),sQuery(id+"F0.wireOp",EDGE,"E161.MirrorCS"),sQuery(id+"F0.wireOp",EDGE,"E162.MirrorCS"),sQuery(id+"F0.wireOp",EDGE,"E163.MirrorCS"),sQuery(id+"F0.wireOp",EDGE,"E164.MirrorCS"),sQuery(id+"F0.wireOp",EDGE,"E165.MirrorCS"),sQuery(id+"F0.wireOp",EDGE,"E166.MirrorCS"),sQuery(id+"F0.wireOp",EDGE,"E167.MirrorCS"),sQuery(id+"F0.wireOp",EDGE,"E168.MirrorCS"),sQuery(id+"F0.wireOp",EDGE,"E169.MirrorCS"),sQuery(id+"F0.wireOp",EDGE,"E171"),sQuery(id+"F0.wireOp",EDGE,"E173.MirrorCS"),sQuery(id+"F0.wireOp",EDGE,"E174.MirrorCS"),sQuery(id+"F0.wireOp",EDGE,"E175.MirrorCS"),sQuery(id+"F0.wireOp",EDGE,"E176.MirrorCS"),sQuery(id+"F0.wireOp",EDGE,"E177.MirrorCS"),sQuery(id+"F0.wireOp",EDGE,"E178.MirrorCS"),sQuery(id+"F0.wireOp",EDGE,"E179.MirrorCS"),sQuery(id+"F0.wireOp",EDGE,"E180.MirrorCS"),sQuery(id+"F0.wireOp",EDGE,"E181.MirrorCS"),sQuery(id+"F0.wireOp",EDGE,"E182.MirrorCS"),sQuery(id+"F0.wireOp",EDGE,"E183.MirrorCS"),sQuery(id+"F0.wireOp",EDGE,"E187"),sQuery(id+"F0.wireOp",EDGE,"E188.MirrorCS"),sQuery(id+"F0.wireOp",EDGE,"E189.MirrorCS"),sQuery(id+"F0.wireOp",EDGE,"E190.MirrorCS"),sQuery(id+"F0.wireOp",EDGE,"E191.MirrorCS"),sQuery(id+"F0.wireOp",EDGE,"E192.MirrorCS"),sQuery(id+"F0.wireOp",EDGE,"E193.MirrorCS"),sQuery(id+"F0.wireOp",EDGE,"E194.MirrorCS"),sQuery(id+"F0.wireOp",EDGE,"E195.MirrorCS"),sQuery(id+"F0.wireOp",EDGE,"E196.MirrorCS"),sQuery(id+"F0.wireOp",EDGE,"E197.MirrorCS"),sQuery(id+"F0.wireOp",EDGE,"E198.MirrorCS"),sQuery(id+"F0.wireOp",EDGE,"E200"),sQuery(id+"F0.wireOp",EDGE,"E201.MirrorCS"),sQuery(id+"F0.wireOp",EDGE,"E202.MirrorCS"),sQuery(id+"F0.wireOp",EDGE,"E203.MirrorCS"),sQuery(id+"F0.wireOp",EDGE,"E204.MirrorCS"),sQuery(id+"F0.wireOp",EDGE,"E205.MirrorCS"),sQuery(id+"F0.wireOp",EDGE,"E206.MirrorCS"),sQuery(id+"F0.wireOp",EDGE,"E207.MirrorCS"),sQuery(id+"F0.wireOp",EDGE,"E208.MirrorCS"),sQuery(id+"F0.wireOp",EDGE,"E209.MirrorCS"),sQuery(id+"F0.wireOp",EDGE,"E210.MirrorCS"),sQuery(id+"F0.wireOp",EDGE,"E211.MirrorCS"),sQuery(id+"F0.wireOp",EDGE,"E214"),sQuery(id+"F0.wireOp",EDGE,"E215"),sQuery(id+"F0.wireOp",EDGE,"E216"),subQ4,subQ2,subQ5,subQ1,subQ0,subQ11,subQ10,subQ9,subQ8,subQ7,subQ6,sQuery(id+"F0.wireOp",EDGE,"E230"),sQuery(id+"F0.wireOp",EDGE,"E234")])],"isStart":true});Q1=makeQuery(id+"F3.boolean.opBoolean","SPLIT",FACE,{"disambiguationData":[TD([makeQuery(id+"F3.opExtrude","SWEPT_FACE",FACE,{"disambiguationData":[OSD([subQ4])]})])],"derivedFrom":subQ15});}
            extrude(context, id + "F11", {"entities" : qUnion([Q0]), "operationType" : NewBodyOperationType.REMOVE, "endBound" : BoundingType.UP_TO_SURFACE, "oppositeDirection" : true, "depth" : 25.4 * mm, "endBoundEntityFace" : qUnion([Q1]), "offsetDistance" : 25.4 * mm});
        }
    });
